# Revit family: 102.603.171_Arres 3.0 Premium (325Wp)
name_source: partatom
category: Allgemeines Modell
units: mm (PartAtom-declared; Revit-internal decimal feet)

## family parameters
Arbeitsebenenbasiert = Nein
Beim Laden mit Abzugskörper schneiden = Nein
Bemaßung runder Anschluss = Durchmesser verwenden
Gemeinsam genutzt = Nein
Immer vertikal = Ja
Kann Basisbauteil für Bewehrung sein = Nein
Raumberechnungspunkt = Nein
Teiletyp = Normal

## types (1)
- Norm
    Backsheetfarbe/EVA = schwarz
    Beschreibung = Arres 3.0 Premium (325Wp)
    Breite = 1060 mm
    Gewicht = 22,70 kg
    Hersteller = Solarmarkt GmbH
    Homepage = https://www.arres.ch
    Höhe = 20 mm
    Kabellänge = 900 mm
    Kurzschlusstrom (Ik) = 10,05 A
    Leerlaufspannung (Uoc) = 41,11 V
    Leistung = 325 Wp
    Leistungsgarantie = 25 Jahre
    Leistungstoleranz = -0/+5
    Länge = 1691 mm
    MPP-Spannung (Umpp) = 33,29 V
    MPP-Strom (Impp) = 9,78 A
    Max. Schneelast  = 9 kN
    Max. Systemspannung = 1000 V
    Max. Windsog = 2,40 kN
    Modell = Arres 3.0 Premium (325Wp)
    Modulwirkungsgrad = 19,45 %
    Produktgarantie = 10 Jahre
    Rahmenfarbe = schwarz
    Steckertyp = Stäubli MC4
    System = Indach
    Temperaturkoeffizient (TKp) = -0,38 %/K
    Trafo erfoderlich = nein
    URL = https://www.solarmarkt.ch
    Vorgabe-Ansicht = 0 mm  [stored 0 ft]
    Zelltyp = Momokristallin

note: [stored X ft] marks values corroborated as IEEE doubles in the binary element streams (Revit-internal decimal feet)
